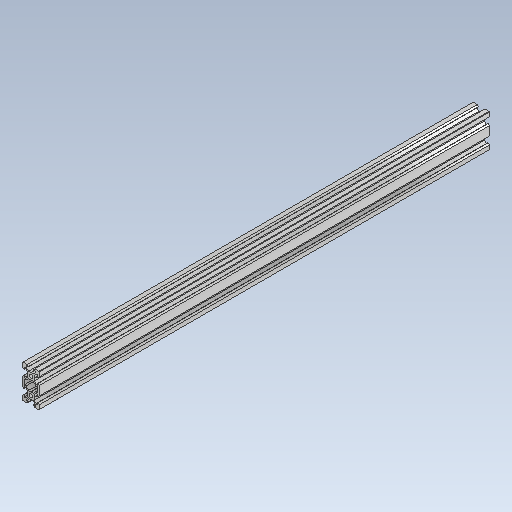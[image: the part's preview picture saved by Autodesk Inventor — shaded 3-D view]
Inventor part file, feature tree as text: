
AUTODESK INVENTOR PART (.ipt)
format: ipt  version: 2020 (Build 240168000, 168)  size: 230,400 bytes
history: native  units: mm
features: extrude x1, sketch x1
ambient origin geometry x8: Origin, YZ Plane, XZ Plane, XY Plane, X Axis, Y Axis, Z Axis, Center Point
bodies: Solid1 (feature_tree)
feature tree (2):
  extrude  "Extrusion1"  [1 undecoded]
  sketch  "Sketch1"  dims[d0=540.0mm d1=0.0mm]
note: 1 required parameter value undecoded (feature->parameter linkage not recoverable at this tier; creation-order binding heuristic only, values carry confidence <= 0.55)
